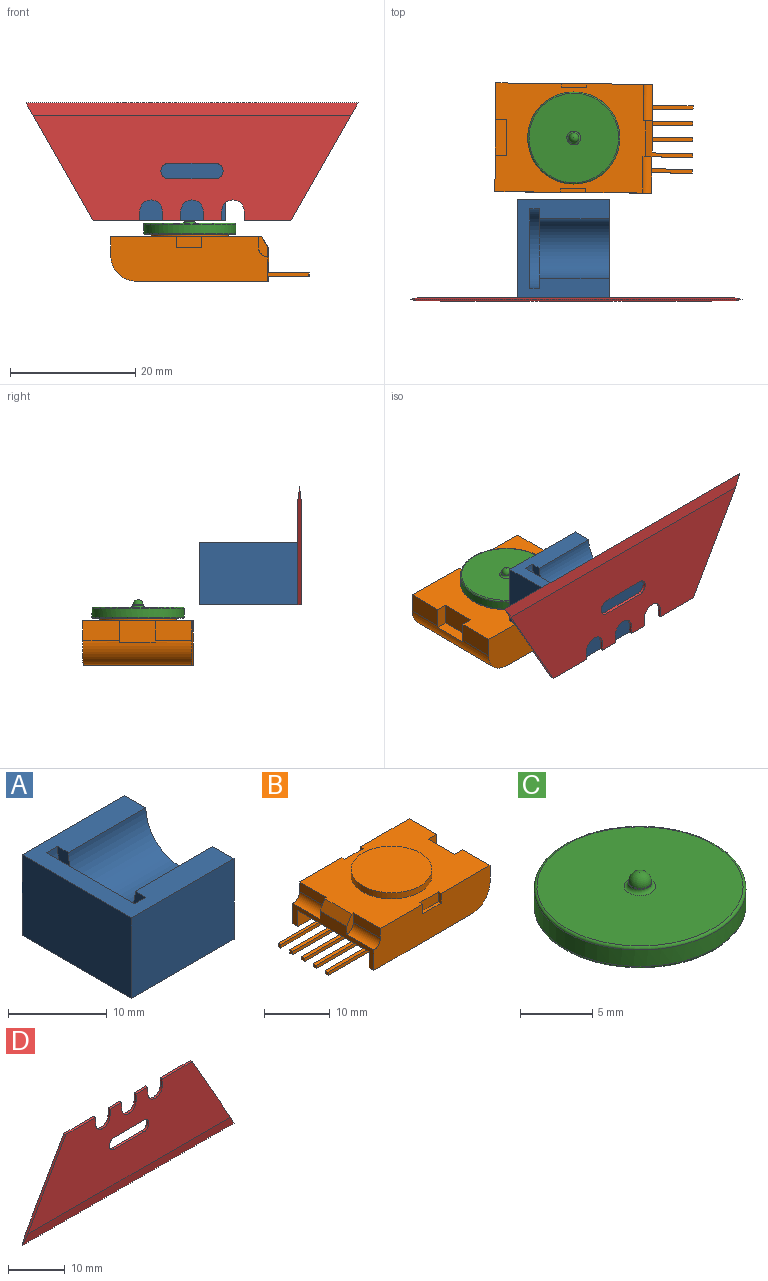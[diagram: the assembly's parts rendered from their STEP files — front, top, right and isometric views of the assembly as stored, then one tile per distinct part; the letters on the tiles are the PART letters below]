
ASSEMBLY  parts=4 mates=4
PART A: 10 faces, bbox 14.7x15.7x10 mm
  f0: plane 15.7x14.71mm, normal (0,0,-1), area 231mm2, adj f2,f4,f7,f9
  f1: plane 15.7x14.71mm, normal (0,0,1), area 104mm2, adj f2,f3,f4,f5,f6,f7,f8,f9
  f2: plane 14.71x10mm, normal (0,-1,0), area 147.1mm2, adj f0,f1,f7,f9
  f3: cylinder r=4.8mm len=11.13mm, axis (1,0,0), area 167.8mm2, adj f1,f6,f7
  f4: plane 14.71x10mm, normal (0,1,0), area 147.1mm2, adj f0,f1,f7,f9
  f5: cylinder r=6.35mm len=12.7mm, axis (-1,0,0), area 31.7mm2, adj f1,f6,f8
  f6: plane 12.7x6.35mm, normal (-1,0,0), area 27.1mm2, adj f1,f3,f5
  f7: plane 15.7x10mm, normal (1,0,0), area 120.8mm2, adj f0,f1,f2,f3,f4
  f8: plane 12.7x6.35mm, normal (1,0,0), area 63.3mm2, adj f1,f5
  f9: plane 15.7x10mm, normal (-1,0,0), area 157mm2, adj f0,f1,f2,f4
PART B: 58 faces, bbox 31.5x17.4x8.3 mm
  f0: plane 23.98x17.36mm, normal (0,0,1), area 277.7mm2, adj f1,f2,f5,f7,f9,f11,f12,f13
  f1: plane 25.02x7.1mm, normal (0,1,0), area 162.8mm2, adj f0,f3,f6,f7,f8,f17,f20,f54
  f2: plane 25.02x7.1mm, normal (0,-1,0), area 162.8mm2, adj f0,f3,f5,f6,f8,f15,f19,f50
  f3: plane 17.36x5.3mm, normal (-1,0,0), area 28.3mm2, adj f1,f2,f8,f16,f18,f19,f20,f21
  f4: plane 15.36x3.05mm, normal (-1,0,0), area 44.9mm2, adj f8,f21,f22,f23,f24,f25,f26,f27
  f5: plane 5.83x3.16mm, normal (1,0,0), area 18.4mm2, adj f0,f2,f6,f11
  f6: cylinder r=3.94mm len=17.36mm, axis (0,-1,0), area 106mm2, adj f1,f2,f5,f7,f8,f11,f12,f14
  f7: plane 5.83x3.16mm, normal (1,0,0), area 18.4mm2, adj f0,f1,f6,f12
  f8: plane 21.08x17.36mm, normal (0,0,-1), area 319.9mm2, adj f1,f2,f3,f4,f6,f21,f23
  f9: cylinder r=6.15mm len=12.3mm, axis (0,0,-1), area 44.4mm2, adj f0,f10
  f10: plane 12.3x12.3mm, normal (0,0,1), area 118.8mm2, adj f9
  f11: plane 3.44x1.81mm, normal (0,1,0), area 6.1mm2, adj f0,f5,f6,f13,f14
  f12: plane 3.44x1.81mm, normal (0,-1,0), area 6.1mm2, adj f0,f6,f7,f13,f14
  f13: plane 5.7x3.42mm, normal (1,0,0), area 19.5mm2, adj f0,f11,f12,f14
  f14: plane 5.72x1.81mm, normal (0,0,1), area 10.2mm2, adj f6,f11,f12,f13
  f15: plane 5.81x1.8mm, normal (-1,0,0), area 10.5mm2, adj f0,f2,f16,f19
  f16: plane 3.25x1.45mm, normal (0,-1,0), area 3.3mm2, adj f0,f3,f15,f19,f49
  f17: plane 5.81x1.8mm, normal (-1,0,0), area 10.5mm2, adj f0,f1,f18,f20
  f18: plane 3.25x1.45mm, normal (0,1,0), area 3.3mm2, adj f0,f3,f17,f20,f49
  f19: cylinder r=1.45mm len=5.81mm, axis (0,-1,0), area 13.2mm2, adj f2,f3,f15,f16
  f20: cylinder r=1.45mm len=5.81mm, axis (0,1,0), area 13.2mm2, adj f1,f3,f17,f18
  f21: plane 3.05x3mm, normal (0,1,0), area 9.2mm2, adj f3,f4,f8,f22
  f22: plane 15.36x3mm, normal (0,0,-1), area 46.1mm2, adj f3,f4,f21,f23
  f23: plane 3.05x3mm, normal (0,-1,0), area 9.2mm2, adj f3,f4,f8,f22
  f24: plane 9.48x0.63mm, normal (0,0,1), area 6mm2, adj f4,f25,f27,f28
  f25: plane 9.48x0.61mm, normal (0,1,0), area 5.8mm2, adj f4,f24,f26,f28
  f26: plane 9.48x0.63mm, normal (0,0,-1), area 6mm2, adj f4,f25,f27,f28
  f27: plane 9.48x0.61mm, normal (0,-1,0), area 5.8mm2, adj f4,f24,f26,f28
  f28: plane 0.63x0.61mm, normal (-1,0,0), area 0.4mm2, adj f24,f25,f26,f27
  f29: plane 9.48x0.63mm, normal (0,0,1), area 6mm2, adj f4,f30,f32,f33
  f30: plane 9.48x0.61mm, normal (0,1,0), area 5.8mm2, adj f4,f29,f31,f33
  f31: plane 9.48x0.63mm, normal (0,0,-1), area 6mm2, adj f4,f30,f32,f33
  f32: plane 9.48x0.61mm, normal (0,-1,0), area 5.8mm2, adj f4,f29,f31,f33
  f33: plane 0.63x0.61mm, normal (-1,0,0), area 0.4mm2, adj f29,f30,f31,f32
  f34: plane 9.48x0.61mm, normal (0,1,0), area 5.8mm2, adj f4,f35,f37,f38
  f35: plane 9.48x0.63mm, normal (0,0,-1), area 6mm2, adj f4,f34,f36,f38
  f36: plane 9.48x0.61mm, normal (0,-1,0), area 5.8mm2, adj f4,f35,f37,f38
  f37: plane 9.48x0.63mm, normal (0,0,1), area 6mm2, adj f4,f34,f36,f38
  f38: plane 0.63x0.61mm, normal (-1,0,0), area 0.4mm2, adj f34,f35,f36,f37
  f39: plane 9.48x0.61mm, normal (0,1,0), area 5.8mm2, adj f4,f40,f42,f43
  f40: plane 9.48x0.63mm, normal (0,0,-1), area 6mm2, adj f4,f39,f41,f43
  f41: plane 9.48x0.61mm, normal (0,-1,0), area 5.8mm2, adj f4,f40,f42,f43
  f42: plane 9.48x0.63mm, normal (0,0,1), area 6mm2, adj f4,f39,f41,f43
  f43: plane 0.63x0.61mm, normal (-1,0,0), area 0.4mm2, adj f39,f40,f41,f42
  f44: plane 9.48x0.61mm, normal (0,1,0), area 5.8mm2, adj f4,f45,f47,f48
  f45: plane 9.48x0.63mm, normal (0,0,-1), area 6mm2, adj f4,f44,f46,f48
  f46: plane 9.48x0.61mm, normal (0,-1,0), area 5.8mm2, adj f4,f45,f47,f48
  f47: plane 9.48x0.63mm, normal (0,0,1), area 6mm2, adj f4,f44,f46,f48
  f48: plane 0.63x0.61mm, normal (-1,0,0), area 0.4mm2, adj f44,f45,f46,f47
  f49: plane 5.74x1.8mm, normal (-0.87,0,0.5), area 11.9mm2, adj f0,f3,f16,f18
  f50: plane 4x0.6mm, normal (0,0,1), area 2.4mm2, adj f2,f51,f52,f53
  f51: plane 1.8x0.6mm, normal (-1,0,0), area 1.1mm2, adj f0,f2,f50,f52
  f52: plane 4x1.8mm, normal (0,-1,0), area 7.2mm2, adj f0,f50,f51,f53
  f53: plane 1.8x0.6mm, normal (1,0,0), area 1.1mm2, adj f0,f2,f50,f52
  f54: plane 4x0.6mm, normal (0,0,1), area 2.4mm2, adj f1,f55,f56,f57
  f55: plane 1.8x0.6mm, normal (-1,0,0), area 1.1mm2, adj f0,f1,f54,f57
  f56: plane 1.8x0.6mm, normal (1,0,0), area 1.1mm2, adj f0,f1,f54,f57
  f57: plane 4x1.8mm, normal (0,1,0), area 7.2mm2, adj f0,f54,f55,f56
PART C: 11 faces, bbox 15.9x15.9x3 mm
  f0: plane 14.3x14.3mm, normal (0,0,1), area 156.8mm2, adj f7,f10
  f1: cylinder r=7.35mm len=14.7mm, axis (0,0,-1), area 64.7mm2, adj f7,f8
  f2: plane 14.3x14.3mm, normal (0,0,-1), area 25.8mm2, adj f8,f9
  f3: cylinder r=6.35mm len=12.7mm, axis (0,0,-1), area 23.9mm2, adj f4,f9
  f4: plane 12.7x12.7mm, normal (0,0,-1), area 126.7mm2, adj f3
  f5: sphere r=0.8mm, area 4mm2, adj f6
  f6: cylinder r=0.8mm len=1.6mm, axis (0,0,-1), area 0.5mm2, adj f5,f10
  f7: torus R=7.15mm, axis (0,0,-1), area 14.4mm2, adj f0,f1
  f8: torus R=7.15mm, axis (0,0,1), area 14.4mm2, adj f1,f2
  f9: torus R=6.55mm, axis (0,0,1), area 12.7mm2, adj f2,f3
  f10: torus R=1.1mm, axis (0,0,-1), area 2.7mm2, adj f0,f6
PART D: 23 faces, bbox 53x0.5x18.8 mm
  f0: plane 18.8x10.7mm, normal (-0.87,0,0.49), area 10.2mm2, adj f11,f19,f20,f21,f22
  f1: plane 18.8x10.7mm, normal (0.87,0,0.49), area 10.2mm2, adj f12,f19,f20,f21,f22
  f2: plane 1.5x0.5mm, normal (1,0,0), area 0.8mm2, adj f3,f18,f19,f20
  f3: plane 2.94x0.5mm, normal (0,0,1), area 1.5mm2, adj f2,f4,f19,f20
  f4: plane 1.5x0.5mm, normal (-1,0,0), area 0.8mm2, adj f3,f5,f19,f20
  f5: cylinder r=1.8mm len=3.6mm, axis (0,1,0), area 2.8mm2, adj f4,f6,f19,f20
  f6: plane 1.5x0.5mm, normal (1,0,0), area 0.8mm2, adj f5,f7,f19,f20
  f7: plane 2.94x0.5mm, normal (0,0,1), area 1.5mm2, adj f6,f8,f19,f20
  f8: plane 1.5x0.5mm, normal (-1,0,0), area 0.8mm2, adj f7,f9,f19,f20
  f9: cylinder r=1.8mm len=3.6mm, axis (0,1,0), area 2.8mm2, adj f8,f10,f19,f20
  f10: plane 1.5x0.5mm, normal (1,0,0), area 0.8mm2, adj f9,f11,f19,f20
  f11: plane 7.46x0.5mm, normal (0,0,1), area 3.7mm2, adj f0,f10,f19,f20
  f12: plane 7.46x0.5mm, normal (0,0,1), area 3.7mm2, adj f1,f13,f19,f20
  f13: plane 1.5x0.5mm, normal (-1,0,0), area 0.8mm2, adj f12,f18,f19,f20
  f14: cylinder r=1.26mm len=2.52mm, axis (0,1,0), area 2mm2, adj f15,f17,f19,f20
  f15: plane 7.42x0.5mm, normal (0,0,1), area 3.7mm2, adj f14,f16,f19,f20
  f16: cylinder r=1.26mm len=2.52mm, axis (0,1,0), area 2mm2, adj f15,f17,f19,f20
  f17: plane 7.42x0.5mm, normal (0,0,-1), area 3.7mm2, adj f14,f16,f19,f20
  f18: cylinder r=1.8mm len=3.6mm, axis (0,1,0), area 2.8mm2, adj f2,f13,f19,f20
  f19: plane 50.72x16.8mm, normal (0,-1,0), area 636.4mm2, adj f0,f1,f2,f3,f4,f5,f6,f7
  f20: plane 50.72x16.8mm, normal (0,1,0), area 636.4mm2, adj f0,f1,f2,f3,f4,f5,f6,f7
  f21: plane 53x2mm, normal (0,-0.99,-0.12), area 104.5mm2, adj f0,f1,f19,f22
  f22: plane 53x2mm, normal (0,0.99,-0.12), area 104.5mm2, adj f0,f1,f20,f21
PLACE A t=(9.4,-0.68,-25.05)mm fixed
PLACE B rot(axis=(0,0,1),179.4deg) t=(29.04,33.42,-27.6)mm
PLACE C rot(axis=(0,0,1),90deg) t=(16.44,24.86,-26.45)mm
PLACE D rot(axis=(0,1,0),180deg) t=(43.3,-0.68,-6.25)mm
MATE cylindrical B.f9 <-> C.f1  axis (0,0,1) through (16.44,24.86,-26.45)mm
MATE planar D.f20 <-> A.f2  axis (0,1,0) through (16.8,-0.68,-15.58)mm
MATE planar B.f9 <-> C.f1  axis (0,0,1) through (16.44,24.86,-26.45)mm
MATE parallel C.f1 <-> A.f0  axis (0,0,1) through (16.44,24.86,-25.45)mm
